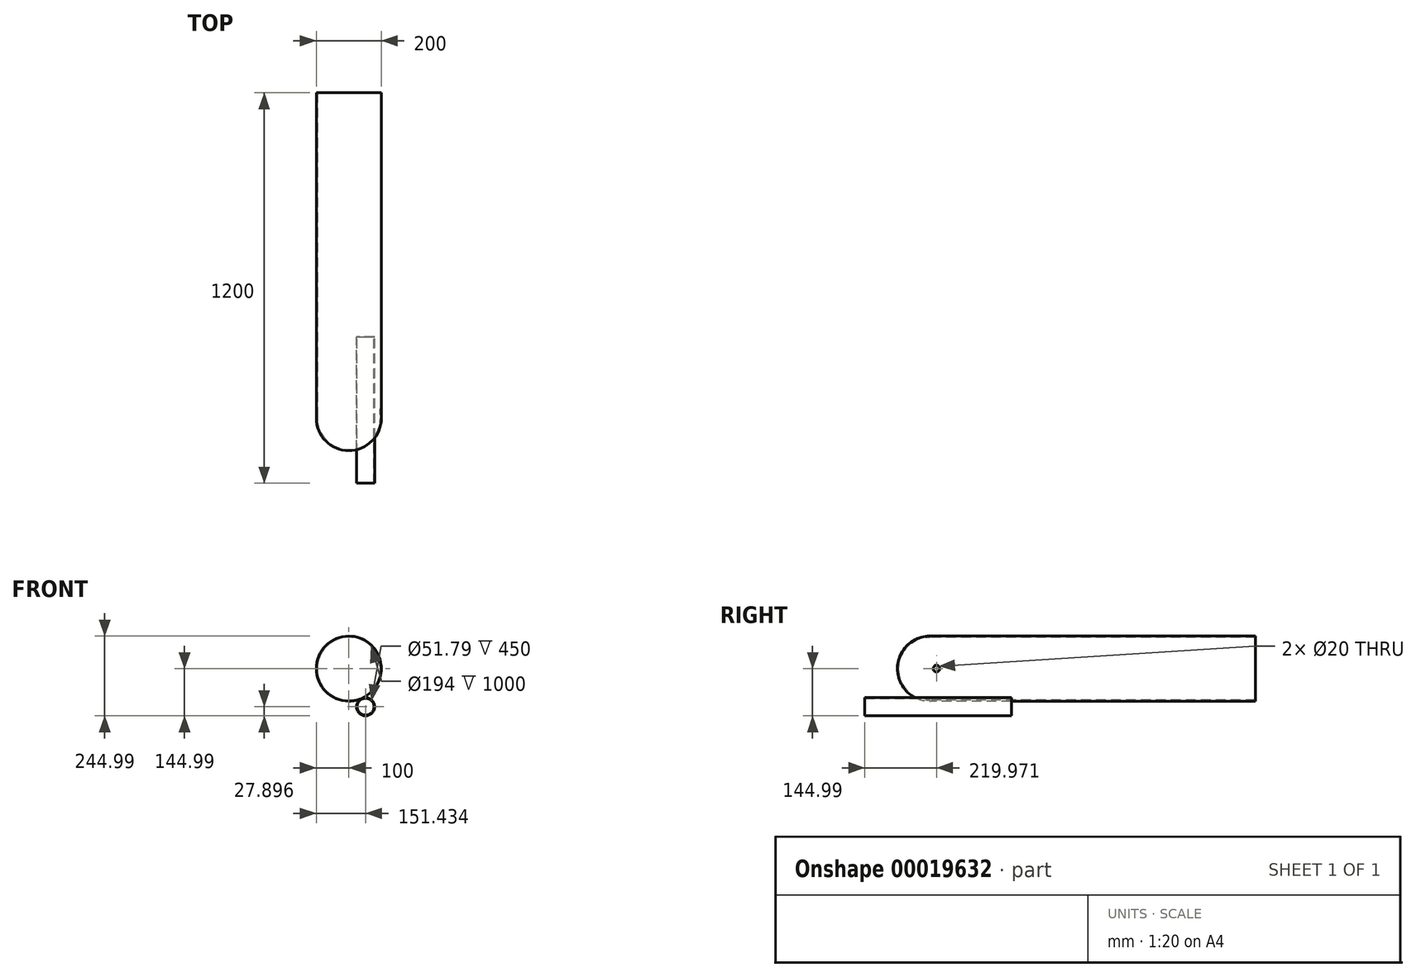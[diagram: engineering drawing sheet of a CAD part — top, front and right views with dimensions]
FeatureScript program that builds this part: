
annotation { "Feature Type Name" : "Feature", "Feature Type Description" : "" }
export const myFeature = defineFeature(function(context is Context, id is Id, definition is map)
    precondition{}
    {
        {
            var Q0;
            Q0=qCreatedBy(makeId("Front.planeOp"),FACE);
            var sketch = newSketch(context, id + "F0", { "sketchPlane" : qUnion([Q0])});
            skCircle(sketch, "E0", {"center": v(0, 0) * mm, "radius": 100 * mm});
            skCircle(sketch, "E1", {"center": v(0, 0) * mm, "radius": 97 * mm});
            skSolve(sketch);
        }
        {
            var Q0;
            Q0 = qSketchRegion(id + "F0", true);
            extrude(context, id + "F1", {"entities" : qUnion([Q0]), "oppositeDirection" : true, "depth" : 1000 * mm});
        }
        {
            var Q0;
            Q0=qCreatedBy(makeId("Right.planeOp"),FACE);
            var sketch = newSketch(context, id + "F2", { "sketchPlane" : qUnion([Q0])});
            skLineSegment(sketch, "E2", {"start": v(0, 100) * mm, "end": v(0, 0) * mm, "construction": true});
            skLineSegment(sketch, "E3", {"start": v(0, 0) * mm, "end": v(-100, 0) * mm, "construction": true});
            skArc(sketch, "E4", {"start": v(0, 100) * mm, "mid": v(-70.71, 70.71) * mm, "end": v(-100, 0) * mm});
            skLineSegment(sketch, "E5", {"start": v(0, 100) * mm, "end": v(78.97, 100) * mm, "construction": true});
            skLineSegment(sketch, "E6", {"start": v(0, 100) * mm, "end": v(0, 97) * mm});
            skLineSegment(sketch, "E7", {"start": v(-100, 0) * mm, "end": v(-97, 0) * mm});
            skArc(sketch, "E8", {"start": v(0, 97) * mm, "mid": v(-68.59, 68.59) * mm, "end": v(-97, 0) * mm});
            skSolve(sketch);
        }
        {
            var Q0;
            Q0 = qSketchRegion(id + "F2", true);
            var Q1;
            Q1=sQuery(id+"F2.wireOp",EDGE,"E3");
            revolve(context, id + "F3", {"entities" : qUnion([Q0]), "axis" : qUnion([Q1]), "revolveType" : RevolveType.FULL});
        }
        {
            var Q0;
            Q0=qCreatedBy(makeId("Front.planeOp"),FACE);
            var sketch = newSketch(context, id + "F4", { "sketchPlane" : qUnion([Q0])});
            skCircle(sketch, "E9", {"center": v(51.43, -117.1) * mm, "radius": 27.9 * mm});
            skCircle(sketch, "E10", {"center": v(51.43, -117.1) * mm, "radius": 25.9 * mm});
            skSolve(sketch);
        }
        {
            var Q0;
            Q0 = qSketchRegion(id + "F4", true);
            extrude(context, id + "F5", {"entities" : qUnion([Q0]), "operationType" : NewBodyOperationType.ADD, "depth" : 200 * mm, "hasSecondDirection" : true, "secondDirectionOppositeDirection" : true, "secondDirectionDepth" : 250 * mm});
        }
        {
            var Q0;
            Q0=qCreatedBy(makeId("Right.planeOp"),FACE);
            var sketch = newSketch(context, id + "F6", { "sketchPlane" : qUnion([Q0])});
            skCircle(sketch, "E11", {"center": v(19.97, 0) * mm, "radius": 10 * mm});
            skSolve(sketch);
        }
        {
            var Q0;
            Q0 = qSketchRegion(id + "F6", true);
            extrude(context, id + "F7", {"entities" : qUnion([Q0]), "operationType" : NewBodyOperationType.REMOVE, "endBound" : BoundingType.SYMMETRIC, "depth" : 500 * mm});
        }
    });
